# Revit family: MG FERRY
name_source: partatom
category: Aparatos sanitarios
revit_build: Autodesk Revit 2016 (Build: 20150220_1215(x64)
units: mm (PartAtom-declared; Revit-internal decimal feet)

## family parameters
Compartido = No
Corte con vacíos al cargar = No
Cota de conector redondo = Diámetro de uso
Número OmniClass = 23.45.00.00
Punto de cálculo de habitación = No
Se basa en plano de trabajo = No
Siempre vertical = Sí
Tipo de pieza = Normal
Título OmniClass = Sanitary, Laundry, and Cleaning Equipment

## types (1)
- MG FERRY
    Certification = http://www.helvex.com.mx
    Comentarios de tipo = SANIVEX
    Conexión AF = Sí
    Data Sheet = http://www.helvex.com.mx
    Descripción = Travis Flush Washout Urinal
    Fabricante = HELVEX
    Features = Hydraulic Seal, Includes Gasket And Spud; Includes Two Settings Kits; Includes Stainless Steel Drain; Water Saving; Requires 0.26 gpf Or 0.13 gpf
    High Gloss Ceramic = High Gloss Ceramic
    Inlet Threads = Feeding: ¾" (19 mm) Flush: 2" 11 - ½ NPT
    Instructive = http://www.helvex.com.mx
    Max. Working Pressure = 85.3 psi
    Min. Working Pressure = 14.2 psi
    Modelo = MG-2
    Note = CNCP Certified
    Total Height = 26"
    Total Length = 19"
    Total Width = 14"
    URL = http://www.helvex.com.mx

## geometry (parser evidence)
native form markers: Sweep x3
no freeform markers — native parametric forms only
